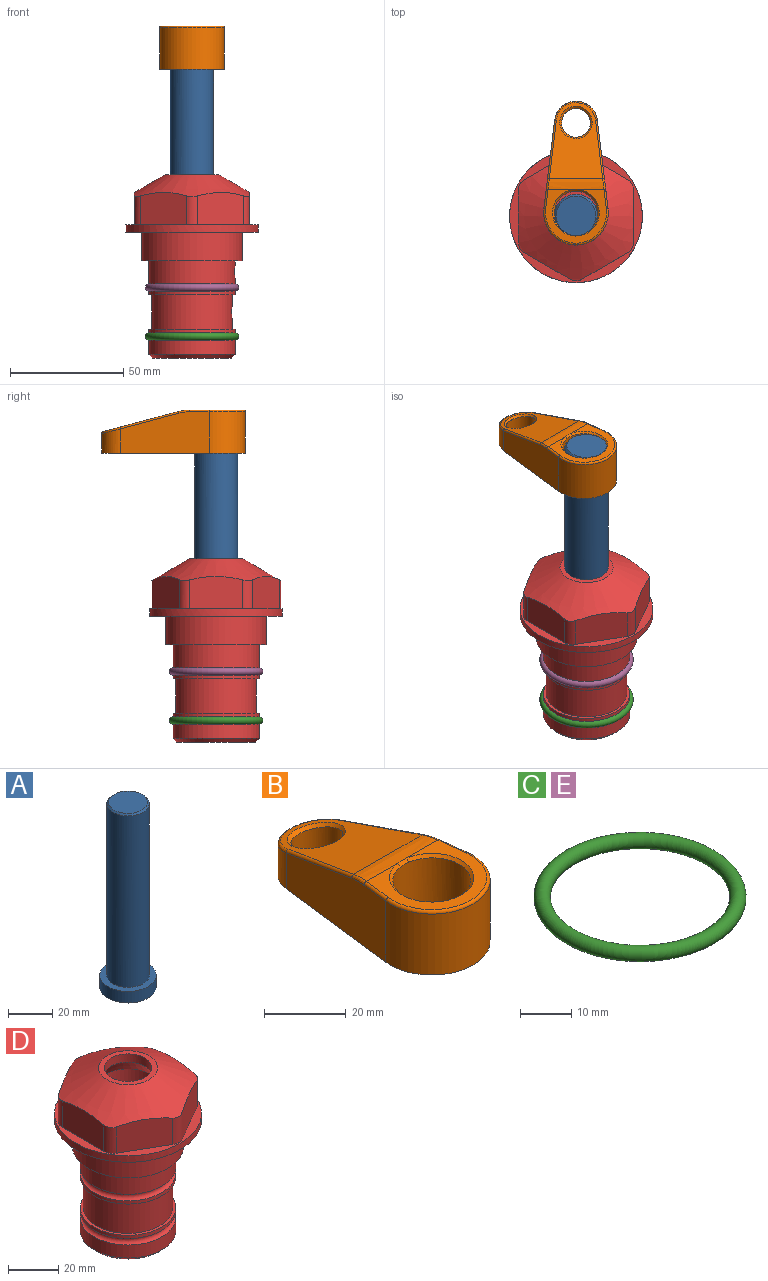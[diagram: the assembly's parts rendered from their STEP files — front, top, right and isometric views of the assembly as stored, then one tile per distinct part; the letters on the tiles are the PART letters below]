
ASSEMBLY  parts=5 mates=4
PART A: 6 faces, bbox 25.4x25.4x101.6 mm
  f0: plane 17.46x17.46mm, normal (0,0,1), area 239.5mm2, adj f5
  f1: plane 25.4x25.4mm, normal (0,0,-1), area 506.7mm2, adj f2
  f2: cylinder r=12.7mm len=25.4mm, axis (0,0,1), area 506.7mm2, adj f1,f3
  f3: plane 25.4x25.4mm, normal (0,0,1), area 221.7mm2, adj f2,f4
  f4: cylinder r=9.53mm len=94.46mm, axis (0,0,1), area 5653mm2, adj f3,f5
  f5: cone r=8.73mm half-angle=45deg, axis (0,0,-1), area 64.4mm2, adj f0,f4
PART B: 31 faces, bbox 31.7x65.5x19.8 mm
  f0: plane 39.12x18.26mm, normal (0.99,0.12,0), area 612.2mm2, adj f1,f4,f7,f11,f13,f15
  f1: cylinder r=9.53mm len=18.91mm, axis (0,0,-1), area 296.1mm2, adj f0,f2,f7,f17
  f2: plane 39.12x18.26mm, normal (-0.99,0.12,0), area 612.2mm2, adj f1,f4,f7,f12,f14,f16
  f3: cylinder r=6.35mm len=12.7mm, axis (0,0,-1), area 362.4mm2, adj f7,f18
  f4: cylinder r=14.29mm len=28.58mm, axis (0,0,-1), area 882.2mm2, adj f0,f2,f7,f10
  f5: cylinder r=9.53mm len=19.05mm, axis (0,0,-1), area 1092.6mm2, adj f7,f19,f20
  f6: plane 26.99x23.69mm, normal (0,0,1), area 216.2mm2, adj f9,f10,f11,f12,f19
  f7: plane 63.5x28.58mm, normal (0,0,-1), area 661.8mm2, adj f0,f1,f2,f3,f4,f5,f22,f23
  f8: plane 33.52x23.6mm, normal (0,0.26,0.97), area 486mm2, adj f9,f15,f16,f17,f18
  f9: cylinder r=19.05mm len=24.72mm, axis (1,0,0), area 120.4mm2, adj f6,f8,f13,f14,f20
  f10: torus R=13.49mm, axis (0,0,1), area 59mm2, adj f4,f6,f11,f12
  f11: cylinder r=0.79mm len=8.67mm, axis (0.12,-0.99,0), area 10.8mm2, adj f0,f6,f10,f13
  f12: cylinder r=0.79mm len=8.67mm, axis (0.12,0.99,0), area 10.8mm2, adj f2,f6,f10,f14
  f13: bspline ~4.95x1.42mm, area 6.1mm2, adj f0,f9,f11,f15
  f14: bspline ~4.95x1.42mm, area 6.1mm2, adj f2,f9,f12,f16
  f15: cylinder r=0.79mm len=25.95mm, axis (0.12,-0.96,0.26), area 32.9mm2, adj f0,f8,f13,f17
  f16: cylinder r=0.79mm len=25.95mm, axis (0.12,0.96,-0.26), area 32.9mm2, adj f2,f8,f14,f17
  f17: bspline ~18.91x8.38mm, area 30mm2, adj f1,f8,f15,f16
  f18: bspline ~14.29x14.29mm, area 48.3mm2, adj f3,f8
  f19: cone r=9.53mm half-angle=45deg, axis (0,0,1), area 66.5mm2, adj f5,f6,f20
  f20: bspline ~3.22x0.96mm, area 3.5mm2, adj f5,f9,f19
  f21: plane 2.75x2.72mm, normal (0,0,-1), area 2.9mm2, adj f23,f25,f28
  f22: plane 23.05x15.88mm, normal (-0.99,-0.12,0), area 323.6mm2, adj f7,f25,f26,f27,f28,f29
  f23: plane 23.05x15.88mm, normal (0.99,-0.12,0), area 323.6mm2, adj f7,f21,f25,f27,f28,f30
  f24: cylinder r=9.53mm len=10.69mm, axis (0,0,-1), area 114.7mm2, adj f7,f27,f29,f30
  f25: cylinder r=12.7mm len=20.59mm, axis (0,0,-1), area 381.1mm2, adj f7,f21,f22,f23,f26,f28
  f26: plane 2.75x2.72mm, normal (0,0,-1), area 2.9mm2, adj f22,f25,f28
  f27: plane 19.72x18.37mm, normal (0,-0.26,-0.97), area 291.8mm2, adj f22,f23,f24,f28,f29,f30
  f28: cylinder r=15.88mm len=19.92mm, axis (1,0,0), area 54.8mm2, adj f21,f22,f23,f25,f26,f27
  f29: cylinder r=1.59mm len=11mm, axis (0,0,-1), area 34.7mm2, adj f7,f22,f24,f27
  f30: cylinder r=1.59mm len=11mm, axis (0,0,-1), area 34.7mm2, adj f7,f23,f24,f27
PART C: 1 faces, bbox 44.7x44.7x3.2 mm
  f0: torus R=19.05mm, axis (0,0,1), area 1193.9mm2
PART D: 36 faces, bbox 58.7x58.7x81 mm
  f0: cylinder r=17.78mm len=35.56mm, axis (0,0,1), area 1670.8mm2, adj f23,f24,f31
  f1: cylinder r=19.05mm len=38.1mm, axis (0,0,1), area 1191.9mm2, adj f26,f27,f30
  f2: plane 58.66x58.66mm, normal (0,0,-1), area 1150.6mm2, adj f3,f28
  f3: cylinder r=29.33mm len=58.66mm, axis (0,0,-1), area 585.1mm2, adj f2,f4
  f4: plane 58.66x58.66mm, normal (0,0,1), area 475.9mm2, adj f3,f5,f6,f7,f8,f9,f10,f11
  f5: plane 20.32x14.34mm, normal (-0.5,0.87,0), area 324.4mm2, adj f4,f15,f16,f17
  f6: plane 20.32x14.34mm, normal (0.5,0.87,0), area 324.4mm2, adj f4,f14,f15,f17
  f7: plane 23.48x14.34mm, normal (1,0,0), area 324.4mm2, adj f4,f13,f14,f17
  f8: plane 20.32x14.34mm, normal (0.5,-0.87,0), area 324.4mm2, adj f4,f12,f13,f17
  f9: plane 20.32x14.34mm, normal (-0.5,-0.87,0), area 324.4mm2, adj f4,f11,f12,f17
  f10: plane 23.48x14.34mm, normal (-1,0,0), area 324.4mm2, adj f4,f11,f16,f17
  f11: cylinder r=5.08mm len=12.85mm, axis (0,0,-1), area 67.2mm2, adj f4,f9,f10,f17
  f12: cylinder r=5.08mm len=12.85mm, axis (0,0,-1), area 67.2mm2, adj f4,f8,f9,f17
  f13: cylinder r=5.08mm len=12.85mm, axis (0,0,-1), area 67.2mm2, adj f4,f7,f8,f17
  f14: cylinder r=5.08mm len=12.85mm, axis (0,0,-1), area 67.2mm2, adj f4,f6,f7,f17
  f15: cylinder r=5.08mm len=12.85mm, axis (0,0,-1), area 67.2mm2, adj f4,f5,f6,f17
  f16: cylinder r=5.08mm len=12.85mm, axis (0,0,-1), area 67.2mm2, adj f4,f5,f10,f17
  f17: cone r=11.73mm half-angle=60deg, axis (0,0,-1), area 2071.8mm2, adj f5,f6,f7,f8,f9,f10,f11,f12
  f18: plane 23.46x23.46mm, normal (0,0,1), area 147.4mm2, adj f17,f35
  f19: plane 34.93x34.93mm, normal (0,0,-1), area 958mm2, adj f29
  f20: cylinder r=19.05mm len=38.1mm, axis (0,0,1), area 760.1mm2, adj f21,f29
  f21: torus R=19.05mm, axis (0,0,1), area 565.3mm2, adj f20,f22
  f22: cylinder r=19.05mm len=38.1mm, axis (0,0,1), area 190mm2, adj f21,f23
  f23: plane 38.1x38.1mm, normal (0,0,1), area 146.9mm2, adj f0,f22
  f24: plane 38.1x38.1mm, normal (0,0,-1), area 146.9mm2, adj f0,f25
  f25: cylinder r=19.05mm len=38.1mm, axis (0,0,1), area 190mm2, adj f24,f26
  f26: torus R=19.05mm, axis (0,0,1), area 565.3mm2, adj f1,f25
  f27: plane 44.45x44.45mm, normal (0,0,-1), area 411.7mm2, adj f1,f28
  f28: cylinder r=22.23mm len=44.45mm, axis (0,0,1), area 1773.5mm2, adj f2,f27
  f29: cone r=19.05mm half-angle=45deg, axis (0,0,1), area 257.5mm2, adj f19,f20
  f30: cylinder r=3.17mm len=6.75mm, axis (-1,0,0), area 128mm2, adj f1,f33
  f31: cylinder r=3.17mm len=6.35mm, axis (-1,0,0), area 102.5mm2, adj f0,f33
  f32: plane 25.4x25.4mm, normal (0,0,1), area 506.7mm2, adj f33
  f33: cylinder r=12.7mm len=66.42mm, axis (0,0,-1), area 5236.2mm2, adj f30,f31,f32,f34
  f34: cone r=9.53mm half-angle=30deg, axis (0,0,-1), area 443.4mm2, adj f33,f35
  f35: cylinder r=9.53mm len=19.05mm, axis (0,0,-1), area 240.9mm2, adj f18,f34
PART E: same geometry as C
PLACE A t=(-12.91,-8.88,13.16)mm
PLACE B t=(-12.91,-7.46,13.16)mm
PLACE C t=(-12.91,-8.88,-35.99)mm
PLACE D t=(-12.91,-8.88,-14.4)mm fixed
PLACE E t=(-12.91,-8.88,-14.4)mm
MATE fastened C.f0 <-> D.f0  axis (0,0,1) through (-12.91,-8.88,-60.5)mm
MATE cylindrical A.f2 <-> D.f0  axis (0,0,-1) through (-12.91,-8.88,-24.94)mm
MATE fastened D.f0 <-> E.f0  axis (0,0,1) through (-12.91,-8.88,-38.91)mm
MATE fastened A.f2 <-> B.f6  axis (0,0,1) through (-12.91,-8.88,76.66)mm
